annotation { "Feature Type Name" : "Feature", "Feature Type Description" : "" }
export const myFeature = defineFeature(function(context is Context, id is Id, definition is map)
    precondition{}
    {
        {
            var Q0;
            Q0=qCreatedBy(makeId("Front.planeOp"),FACE);
            var sketch = newSketch(context, id + "F0", { "sketchPlane" : qUnion([Q0])});
            skText(sketch, "E0", { "text": "Paige Ngo", "fontName": "Tinos-Regular.ttf"});
            const initialGuessF0  = {"E0": [-0.0499, 0, 1, 0, 0.01707]};
            skSetInitialGuess(sketch, initialGuessF0);
            skSolve(sketch);
        }
        {
            var Q0;
            Q0 = qSketchRegion(id + "F0", true);
            extrude(context, id + "F1", {"entities" : qUnion([Q0]), "depth" : 3 * mm, "offsetDistance" : 25.4 * mm});
        }
        {
            var Q0;
            Q0=qCreatedBy(makeId("Front.planeOp"),FACE);
            var sketch = newSketch(context, id + "F2", { "sketchPlane" : qUnion([Q0])});
            skLineSegment(sketch, "E1.bottom", {"start": v(-50.99, 0) * mm, "end": v(-16.76, 0) * mm});
            skLineSegment(sketch, "E1.top", {"start": v(-50.99, -1.27) * mm, "end": v(-16.76, -1.27) * mm});
            skLineSegment(sketch, "E1.left", {"start": v(-50.99, 0) * mm, "end": v(-50.99, -1.27) * mm});
            skLineSegment(sketch, "E1.right", {"start": v(-16.76, 0) * mm, "end": v(-16.76, -1.27) * mm});
            skLineSegment(sketch, "E2.bottom", {"start": v(-8.9, 0) * mm, "end": v(28.67, 0) * mm});
            skLineSegment(sketch, "E2.top", {"start": v(-8.9, -1.27) * mm, "end": v(28.67, -1.27) * mm});
            skLineSegment(sketch, "E2.left", {"start": v(-8.9, 0) * mm, "end": v(-8.9, -1.27) * mm});
            skLineSegment(sketch, "E2.right", {"start": v(28.67, 0) * mm, "end": v(28.67, -1.27) * mm});
            skLineSegment(sketch, "E3.bottom", {"start": v(36.1, 0) * mm, "end": v(50.4, 0) * mm});
            skLineSegment(sketch, "E3.top", {"start": v(36.1, -1.27) * mm, "end": v(50.4, -1.27) * mm});
            skLineSegment(sketch, "E3.left", {"start": v(36.1, 0) * mm, "end": v(36.1, -1.27) * mm});
            skLineSegment(sketch, "E3.right", {"start": v(50.4, 0) * mm, "end": v(50.4, -1.27) * mm});
            skSolve(sketch);
        }
        {
            var Q0;
            Q0 = qSketchRegion(id + "F2", true);
            extrude(context, id + "F3", {"entities" : qUnion([Q0]), "operationType" : NewBodyOperationType.ADD, "depth" : 3 * mm, "offsetDistance" : 25.4 * mm});
        }
        {
            var Q0;
            Q0=qCreatedBy(makeId("Front.planeOp"),FACE);
            var sketch = newSketch(context, id + "F4", { "sketchPlane" : qUnion([Q0])});
            skLineSegment(sketch, "E4.bottom", {"start": v(-50.99, 16.72) * mm, "end": v(50.4, 16.72) * mm});
            skLineSegment(sketch, "E4.top", {"start": v(-50.99, 15.45) * mm, "end": v(50.4, 15.45) * mm});
            skLineSegment(sketch, "E4.left", {"start": v(-50.99, 16.72) * mm, "end": v(-50.99, 15.45) * mm});
            skLineSegment(sketch, "E4.right", {"start": v(50.4, 16.72) * mm, "end": v(50.4, 15.45) * mm});
            skLineSegment(sketch, "E5.bottom", {"start": v(-48.97, 15.45) * mm, "end": v(-41.94, 15.45) * mm});
            skLineSegment(sketch, "E5.top", {"start": v(-48.97, 15.45) * mm, "end": v(-41.94, 15.45) * mm});
            skLineSegment(sketch, "E5.left", {"start": v(-48.97, 15.45) * mm, "end": v(-48.97, 15.45) * mm});
            skLineSegment(sketch, "E5.right", {"start": v(-41.94, 15.45) * mm, "end": v(-41.94, 15.45) * mm});
            skSolve(sketch);
        }
        {
            var Q0;
            Q0 = qSketchRegion(id + "F4", true);
            extrude(context, id + "F5", {"entities" : qUnion([Q0]), "operationType" : NewBodyOperationType.ADD, "depth" : 3 * mm, "offsetDistance" : 25.4 * mm});
        }
    });